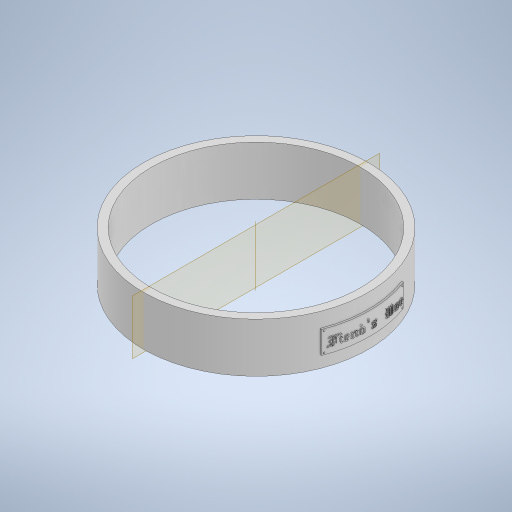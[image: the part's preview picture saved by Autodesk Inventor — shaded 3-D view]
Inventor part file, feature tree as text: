
AUTODESK INVENTOR PART (.ipt)
format: ipt  version: 2023 (Build 270158000, 158)  size: 4,147,200 bytes
history: native  units: in
note: dims shown in document units (in); Inventor stores cm internally (conversion verified against a paired STEP export)
features: emboss x3, pattern_circular x3, other x2, extrude x1, plane x1, fillet x1, sketch x1
ambient origin geometry x8: Origin, YZ Plane, XZ Plane, XY Plane, X Axis, Y Axis, Z Axis, Center Point
bodies: Solid1 (feature_tree)
feature tree (12):
  extrude  "Extrusion1"  Depth=0.3937in
  plane  "Work Plane1"
  other  "Text"
  emboss  "Emboss4"
  emboss  "Emboss5"
  emboss  "Emboss6"
  fillet  "Rivots"  Radius=0.8661in
  pattern_circular  "Circular Pattern1"  Count=6  [1 undecoded]
  pattern_circular  "Circular Pattern2"  [2 undecoded]
  pattern_circular  "Circular Pattern3"  [2 undecoded]
  sketch  "Sketch1"  dims[d0=3.937in d1=3.6614in d2=0.8661in d3=0.0in d4=2.3622in d6=0.4546in d10=0.0in d11=0.3937in d12=1.4567in d19=0.0in d20=0.0in d21=0.0295in d22=0.0in d23=0.0197in d24=0.0in d25=0.0295in d26=0.0295in d27=0.0295in d28=0.0157in d29=0.0in d30=0.0138in d31=0.7874in d32=360.0deg d34=0.7874in d35=360.0deg d37=0.7874in d38=360.0deg d33=0.0in]
  other  "NamePlate"
note: 5 required parameter values undecoded (feature->parameter linkage not recoverable at this tier; creation-order binding heuristic only, values carry confidence <= 0.55)
